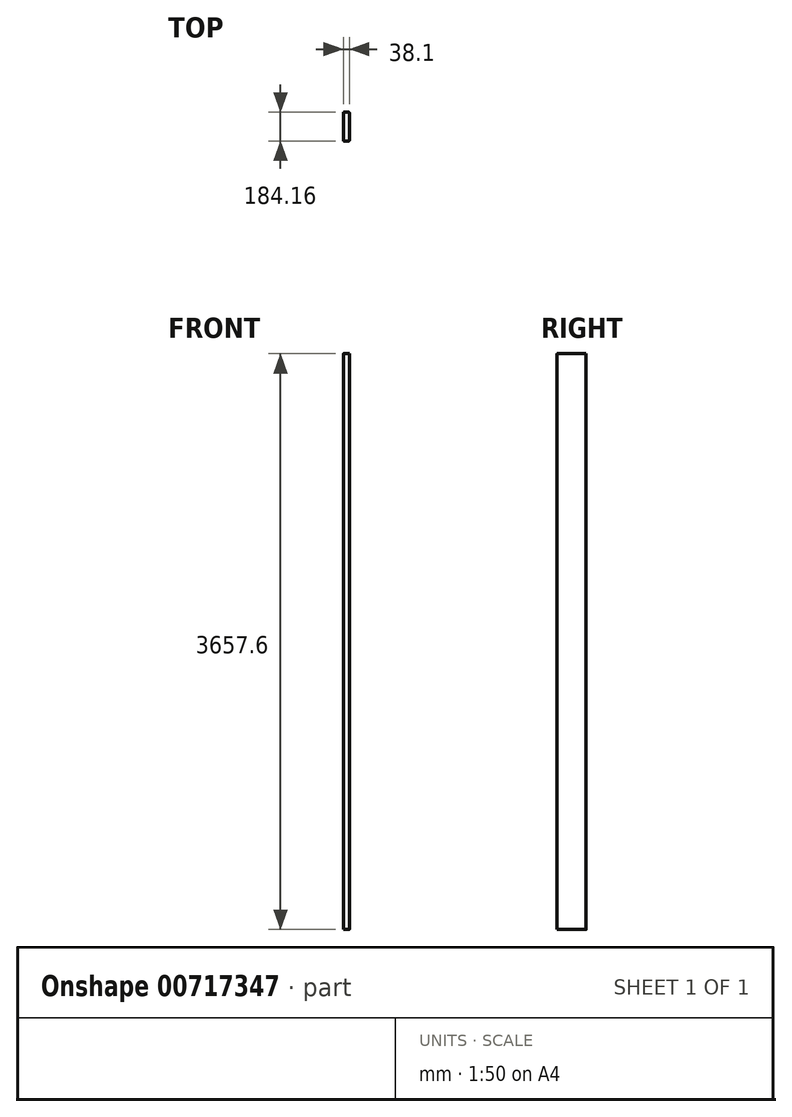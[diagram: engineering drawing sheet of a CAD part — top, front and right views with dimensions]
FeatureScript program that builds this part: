
annotation { "Feature Type Name" : "Feature", "Feature Type Description" : "" }
export const myFeature = defineFeature(function(context is Context, id is Id, definition is map)
    precondition{}
    {
        {
            var Q0;
            Q0=qCreatedBy(makeId("Top.planeOp"),FACE);
            var sketch = newSketch(context, id + "F0", { "sketchPlane" : qUnion([Q0])});
            skLineSegment(sketch, "E0.bottom", {"start": v(-12.7, 92.08) * mm, "end": v(12.7, 92.08) * mm});
            skLineSegment(sketch, "E0.top", {"start": v(-12.7, -92.08) * mm, "end": v(12.7, -92.08) * mm});
            skLineSegment(sketch, "E0.left", {"start": v(-19.05, 85.73) * mm, "end": v(-19.05, -85.73) * mm});
            skLineSegment(sketch, "E0.right", {"start": v(19.05, 85.73) * mm, "end": v(19.05, -85.73) * mm});
            skLineSegment(sketch, "E1", {"start": v(-19.05, -92.08) * mm, "end": v(19.05, 92.08) * mm, "construction": true});
            skPoint(sketch, "E2.visualSharp", {"position": v(19.05, 92.08) * mm});
            skArc(sketch, "E2.filletArc", {"start": v(19.05, 85.73) * mm, "mid": v(17.2, 90.22) * mm, "end": v(12.7, 92.08) * mm});
            skPoint(sketch, "E3.visualSharp", {"position": v(-19.05, 92.08) * mm});
            skArc(sketch, "E3.filletArc", {"start": v(-12.7, 92.08) * mm, "mid": v(-17.2, 90.22) * mm, "end": v(-19.05, 85.73) * mm});
            skPoint(sketch, "E4.visualSharp", {"position": v(-19.05, -92.08) * mm});
            skArc(sketch, "E4.filletArc", {"start": v(-19.05, -85.73) * mm, "mid": v(-17.2, -90.22) * mm, "end": v(-12.7, -92.08) * mm});
            skPoint(sketch, "E5.visualSharp", {"position": v(19.05, -92.08) * mm});
            skArc(sketch, "E5.filletArc", {"start": v(12.7, -92.08) * mm, "mid": v(17.2, -90.22) * mm, "end": v(19.05, -85.73) * mm});
            skSolve(sketch);
        }
        {
            var Q0;
            Q0=makeQuery(id+"F0.imprint","IMPRINT",FACE,{"disambiguationData":[TD([[makeQuery(id+"F0.imprint","IMPRINT",EDGE,{"derivedFrom":sQuery(id+"F0.wireOp",EDGE,"E0.bottom")}),-1.0]])]});
            extrude(context, id + "F1", {"entities" : qUnion([Q0]), "depth" : 3657.6 * mm, "offsetDistance" : 25.4 * mm});
        }
    });
